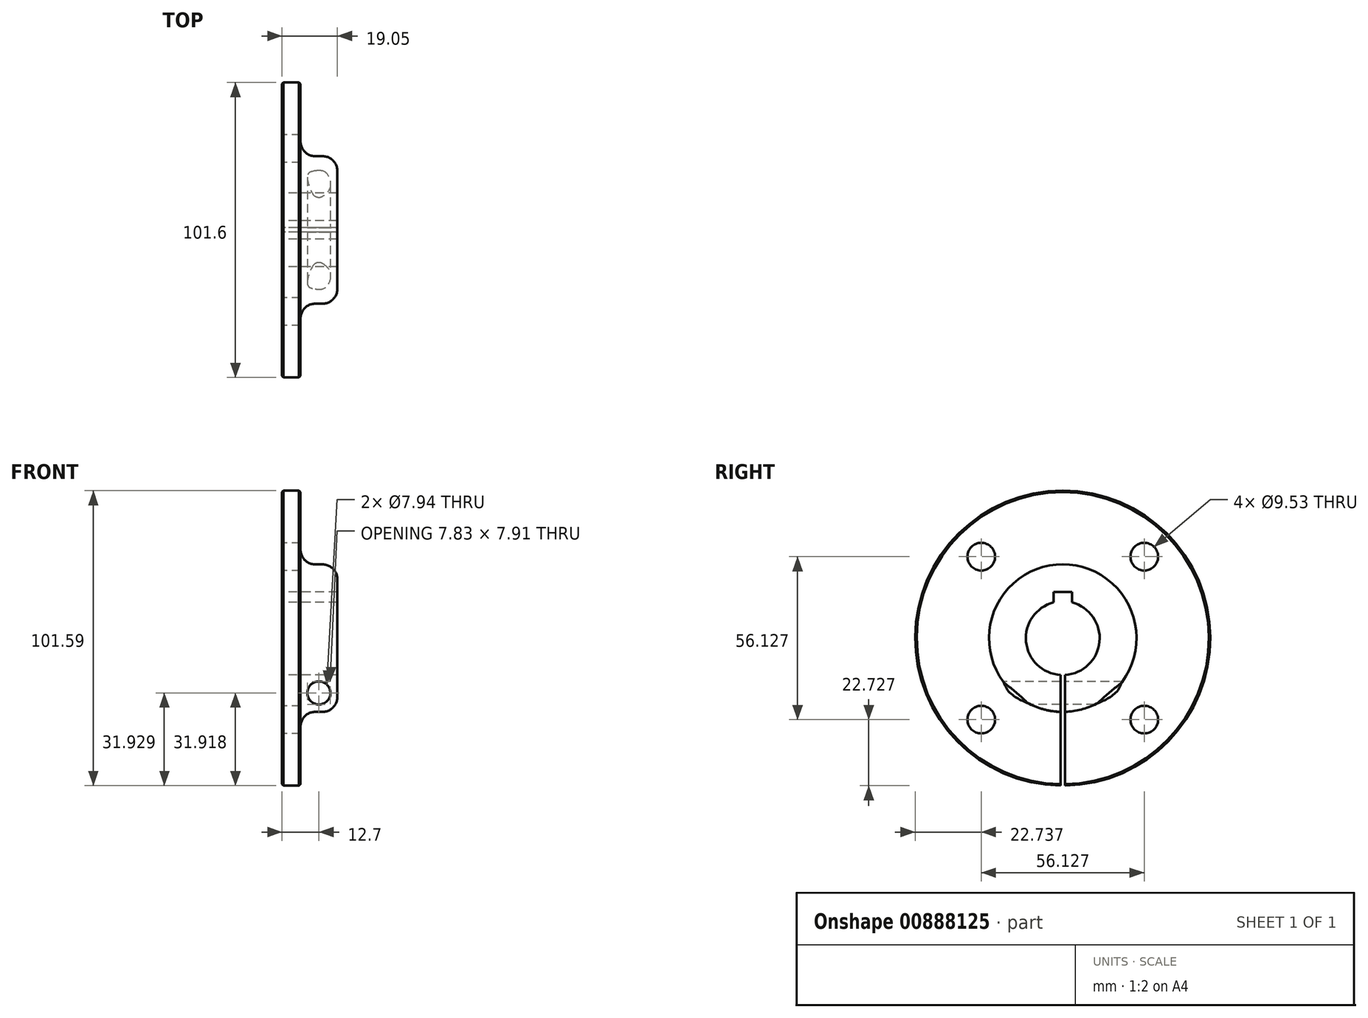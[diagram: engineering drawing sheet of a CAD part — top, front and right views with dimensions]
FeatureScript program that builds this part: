
annotation { "Feature Type Name" : "Feature", "Feature Type Description" : "" }
export const myFeature = defineFeature(function(context is Context, id is Id, definition is map)
    precondition{}
    {
        {
            var Q0;
            Q0=qCreatedBy(makeId("Front.planeOp"),FACE);
            var sketch = newSketch(context, id + "F0", { "sketchPlane" : qUnion([Q0])});
            skLineSegment(sketch, "E0", {"start": v(0, 0) * mm, "end": v(0, 12.7) * mm, "construction": true});
            skLineSegment(sketch, "E1", {"start": v(0, 12.7) * mm, "end": v(0, 50.8) * mm});
            skLineSegment(sketch, "E2", {"start": v(0, 50.8) * mm, "end": v(6.35, 50.8) * mm});
            skLineSegment(sketch, "E3", {"start": v(6.35, 50.8) * mm, "end": v(6.35, 25.4) * mm});
            skLineSegment(sketch, "E4", {"start": v(6.35, 25.4) * mm, "end": v(19.05, 25.4) * mm});
            skLineSegment(sketch, "E5", {"start": v(19.05, 25.4) * mm, "end": v(19.05, 12.7) * mm});
            skLineSegment(sketch, "E6", {"start": v(19.05, 12.7) * mm, "end": v(0, 12.7) * mm});
            skLineSegment(sketch, "E7", {"start": v(0, 0) * mm, "end": v(19.05, 0) * mm, "construction": true});
            skSolve(sketch);
        }
        {
            var Q0;
            Q0 = qSketchRegion(id + "F0", true);
            var Q1;
            Q1=sQuery(id+"F0.wireOp",EDGE,"E7");
            revolve(context, id + "F1", {"surfaceOperationType" : NewSurfaceOperationType.NEW, "entities" : qUnion([Q0]), "axis" : qUnion([Q1]), "revolveType" : RevolveType.FULL});
        }
        {
            var Q0;
            Q0=makeQuery(id+"F1.opRevolve","SWEPT_EDGE",EDGE,{"disambiguationData":[OSD([sQuery(id+"F0.wireOp",EDGE,"E4"),sQuery(id+"F0.wireOp",EDGE,"E5")])]});
            var Q1;
            Q1=makeQuery(id+"F1.opRevolve","SWEPT_EDGE",EDGE,{"disambiguationData":[OSD([sQuery(id+"F0.wireOp",EDGE,"E3"),sQuery(id+"F0.wireOp",EDGE,"E4")])]});
            fillet(context, id + "F2", {"entities" : qUnion([Q0, Q1]), "radius" : 5.08 * mm, "tangentPropagation" : true, "allowEdgeOverflow" : false});
        }
        {
            var Q0;
            Q0=makeQuery(id+"F1.opRevolve","SWEPT_EDGE",EDGE,{"disambiguationData":[OSD([sQuery(id+"F0.wireOp",EDGE,"E2"),sQuery(id+"F0.wireOp",EDGE,"E3")])]});
            var Q1;
            Q1=makeQuery(id+"F1.opRevolve","SWEPT_EDGE",EDGE,{"disambiguationData":[OSD([sQuery(id+"F0.wireOp",EDGE,"E1"),sQuery(id+"F0.wireOp",EDGE,"E2")])]});
            chamfer(context, id + "F3", {"entities" : qUnion([Q0, Q1]), "width" : 0.5 * mm, "tangentPropagation" : true});
        }
        {
            var Q0;
            Q0=makeQuery(id+"F1.opRevolve","SWEPT_FACE",FACE,{"disambiguationData":[OSD([sQuery(id+"F0.wireOp",EDGE,"E1")])]});
            var sketch = newSketch(context, id + "F4", { "sketchPlane" : qUnion([Q0])});
            skLineSegment(sketch, "E8", {"start": v(0, 0) * mm, "end": v(-28.06, 28.06) * mm, "construction": true});
            skCircle(sketch, "E9", {"center": v(-28.06, 28.06) * mm, "radius": 4.76 * mm});
            skCircle(sketch, "E10.1.0", {"center": v(-28.06, -28.06) * mm, "radius": 4.76 * mm});
            skCircle(sketch, "E10.2.0", {"center": v(28.06, -28.06) * mm, "radius": 4.76 * mm});
            skCircle(sketch, "E10.3.0", {"center": v(28.06, 28.06) * mm, "radius": 4.76 * mm});
            skPoint(sketch, "E10.center", {"position": v(0, 0) * mm});
            skLineSegment(sketch, "E11.bottom", {"start": v(3.17, 15.88) * mm, "end": v(-3.17, 15.88) * mm});
            skLineSegment(sketch, "E11.top", {"start": v(3.17, 9.53) * mm, "end": v(-3.17, 9.53) * mm});
            skLineSegment(sketch, "E11.left", {"start": v(3.18, 15.88) * mm, "end": v(3.18, 9.53) * mm});
            skLineSegment(sketch, "E11.right", {"start": v(-3.17, 15.88) * mm, "end": v(-3.17, 9.53) * mm});
            skPoint(sketch, "E11.middle", {"position": v(0, 12.7) * mm});
            skLineSegment(sketch, "E12.bottom", {"start": v(-0.8, 6.99) * mm, "end": v(0.8, 6.99) * mm});
            skLineSegment(sketch, "E12.top", {"start": v(-0.8, -53.46) * mm, "end": v(0.8, -53.46) * mm});
            skLineSegment(sketch, "E12.left", {"start": v(-0.8, 6.99) * mm, "end": v(-0.8, -53.46) * mm});
            skLineSegment(sketch, "E12.right", {"start": v(0.8, 6.99) * mm, "end": v(0.8, -53.46) * mm});
            skPoint(sketch, "E12.middle", {"position": v(0, -23.24) * mm});
            skSolve(sketch);
        }
        {
            var Q0;
            Q0 = qSketchRegion(id + "F4", true);
            extrude(context, id + "F5", {"entities" : qUnion([Q0]), "operationType" : NewBodyOperationType.REMOVE, "endBound" : BoundingType.THROUGH_ALL, "oppositeDirection" : true, "depth" : 25.4 * mm, "offsetDistance" : 25.4 * mm});
        }
        {
            var Q0;
            Q0=qCreatedBy(makeId("Front.planeOp"),FACE);
            var sketch = newSketch(context, id + "F6", { "sketchPlane" : qUnion([Q0])});
            skCircle(sketch, "E13", {"center": v(12.7, -18.87) * mm, "radius": 3.97 * mm});
            skLineSegment(sketch, "E14", {"start": v(0, 0) * mm, "end": v(11.43, 0) * mm, "construction": true});
            skLineSegment(sketch, "E15", {"start": v(11.43, 0) * mm, "end": v(13.97, 0) * mm, "construction": true});
            skLineSegment(sketch, "E16", {"start": v(12.7, 0) * mm, "end": v(12.7, -18.87) * mm, "construction": true});
            skSolve(sketch);
        }
        {
            var Q0;
            Q0 = qSketchRegion(id + "F6", true);
            extrude(context, id + "F7", {"entities" : qUnion([Q0]), "operationType" : NewBodyOperationType.REMOVE, "endBound" : BoundingType.THROUGH_ALL, "oppositeDirection" : true, "depth" : 25.4 * mm, "offsetDistance" : 25.4 * mm, "hasSecondDirection" : true, "secondDirectionBound" : BoundingType.THROUGH_ALL, "secondDirectionOppositeDirection" : false, "secondDirectionDepth" : 25.4 * mm});
        }
    });
